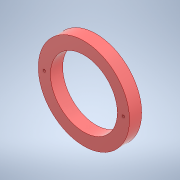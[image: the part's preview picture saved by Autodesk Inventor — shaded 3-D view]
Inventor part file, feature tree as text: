
AUTODESK INVENTOR PART (.ipt)
format: ipt  version: 2020 (Build 240168000, 168)  size: 113,664 bytes
history: native  units: mm
features: extrude x1, sketch x1
ambient origin geometry x8: Origin, YZ Plane, XZ Plane, XY Plane, X Axis, Y Axis, Z Axis, Center Point
bodies: Solid1 (feature_tree)
feature tree (2):
  extrude  "Extrusion1"  Depth=10.0mm
  sketch  "Sketch1"  dims[d0=75.0mm d1=65.0mm d2=2.0mm d3=2.0mm d4=55.0mm d5=10.0mm d6=0.0mm d7=0.872665mm]
